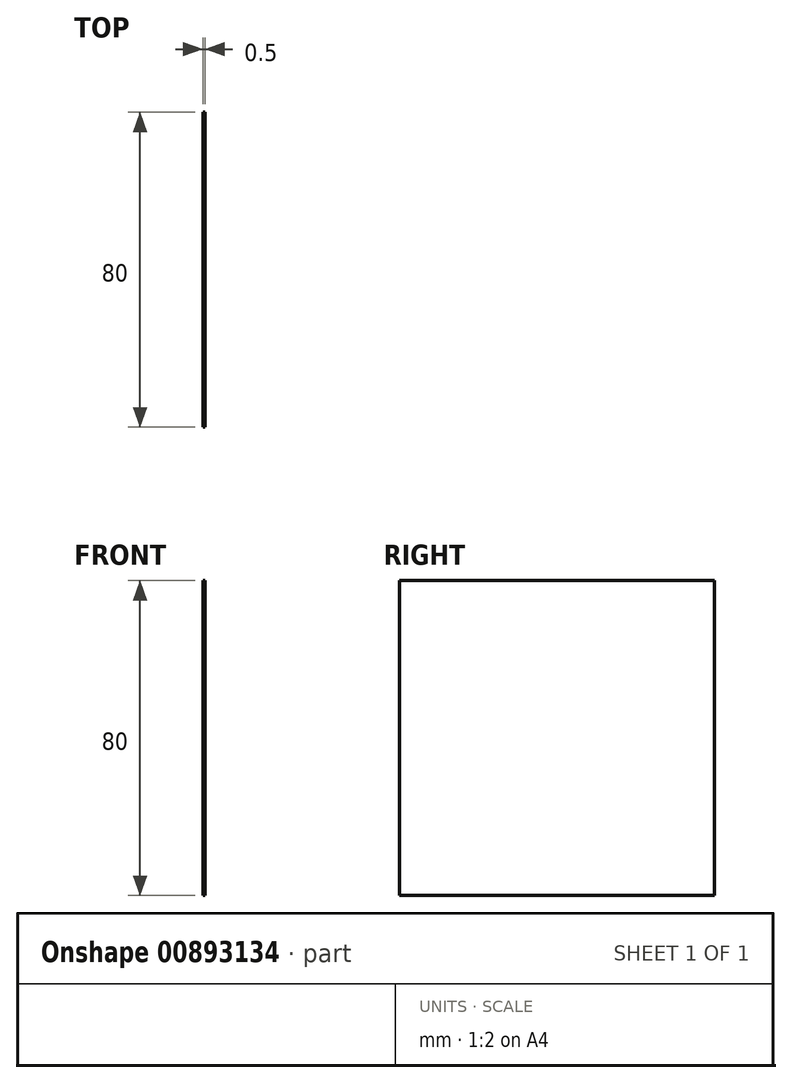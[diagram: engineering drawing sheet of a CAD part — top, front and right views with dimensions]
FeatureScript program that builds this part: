
annotation { "Feature Type Name" : "Feature", "Feature Type Description" : "" }
export const myFeature = defineFeature(function(context is Context, id is Id, definition is map)
    precondition{}
    {
        {
            var Q0;
            Q0=qCreatedBy(makeId("Right.planeOp"),FACE);
            var sketch = newSketch(context, id + "F0", { "sketchPlane" : qUnion([Q0])});
            skLineSegment(sketch, "E0.bottom", {"start": v(0, 0) * mm, "end": v(80, 0) * mm});
            skLineSegment(sketch, "E0.top", {"start": v(0, -80) * mm, "end": v(80, -80) * mm});
            skLineSegment(sketch, "E0.left", {"start": v(0, 0) * mm, "end": v(0, -80) * mm});
            skLineSegment(sketch, "E0.right", {"start": v(80, 0) * mm, "end": v(80, -80) * mm});
            skSolve(sketch);
        }
        {
            var Q0;
            Q0=makeQuery(id+"F0.imprint","IMPRINT",FACE,{"disambiguationData":[TD([[makeQuery(id+"F0.imprint","IMPRINT",EDGE,{"derivedFrom":sQuery(id+"F0.wireOp",EDGE,"E0.bottom")}),-1.0]])]});
            extrude(context, id + "F1", {"entities" : qUnion([Q0]), "depth" : .5 * mm, "offsetDistance" : 25 * mm});
        }
    });
